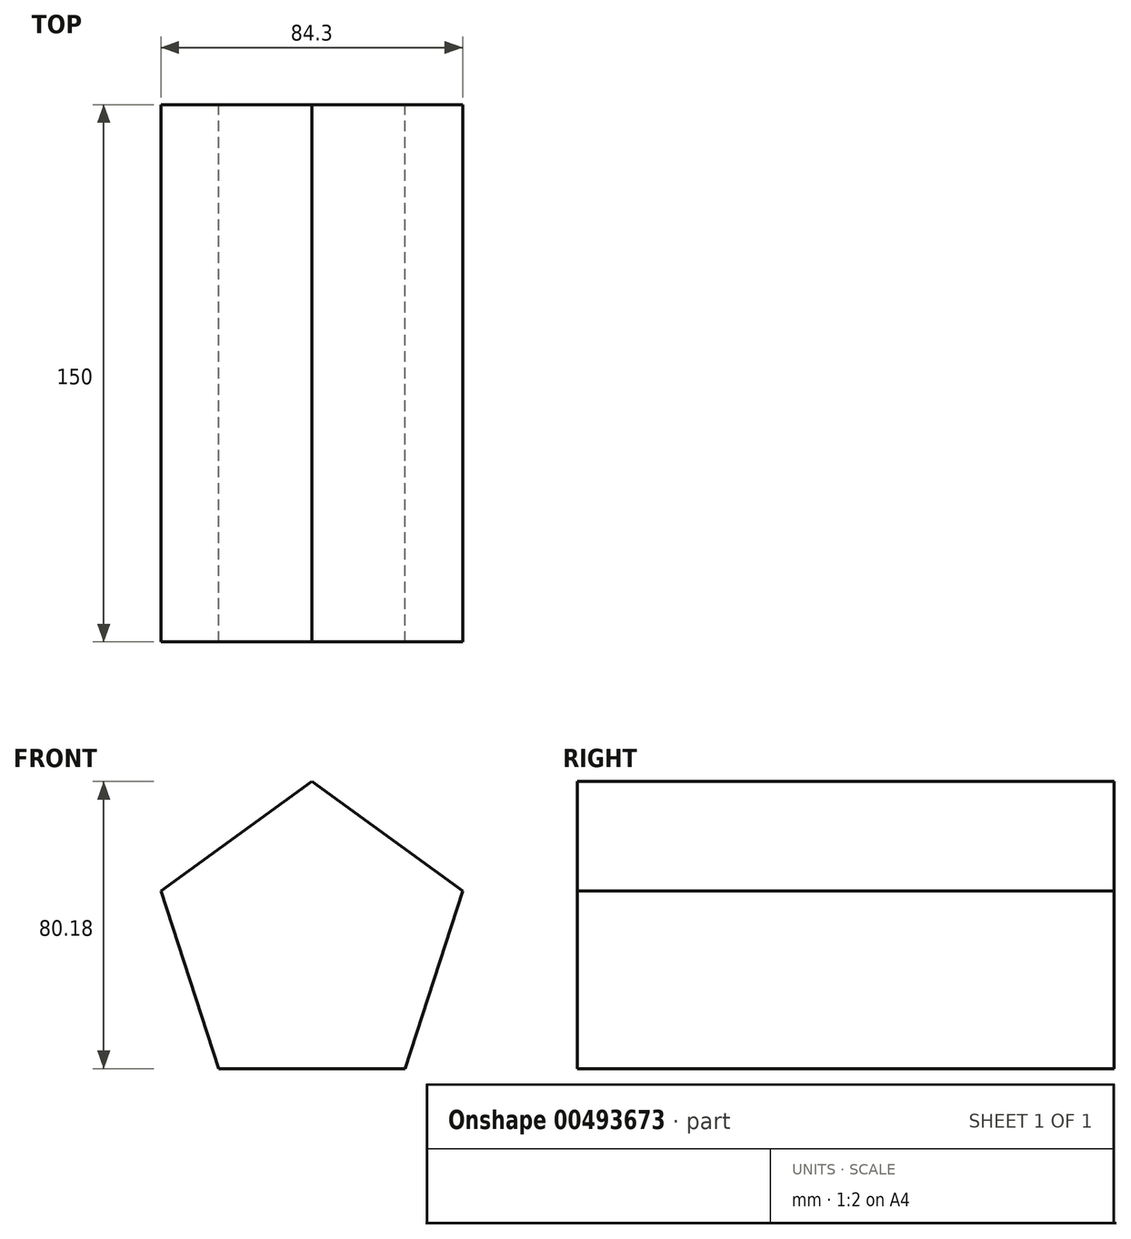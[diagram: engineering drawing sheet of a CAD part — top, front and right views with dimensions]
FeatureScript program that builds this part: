
annotation { "Feature Type Name" : "Feature", "Feature Type Description" : "" }
export const myFeature = defineFeature(function(context is Context, id is Id, definition is map)
    precondition{}
    {
        {
            var Q0;
            Q0=qCreatedBy(makeId("Front.planeOp"),FACE);
            var sketch = newSketch(context, id + "F0", { "sketchPlane" : qUnion([Q0])});
            skCircle(sketch, "E0.cCircle", {"center": v(0, 0) * mm, "radius": 44.32 * mm, "construction": true});
            skLineSegment(sketch, "E0.0", {"start": v(0, 44.32) * mm, "end": v(42.15, 13.7) * mm});
            skLineSegment(sketch, "E0.1", {"start": v(42.15, 13.7) * mm, "end": v(26.05, -35.86) * mm});
            skLineSegment(sketch, "E0.2", {"start": v(26.05, -35.86) * mm, "end": v(-26.05, -35.86) * mm});
            skLineSegment(sketch, "E0.3", {"start": v(-26.05, -35.86) * mm, "end": v(-42.15, 13.7) * mm});
            skLineSegment(sketch, "E0.4", {"start": v(-42.15, 13.7) * mm, "end": v(0, 44.32) * mm});
            skSolve(sketch);
        }
        {
            var Q0;
            Q0=makeQuery(id+"F0.imprint","IMPRINT",FACE,{"disambiguationData":[TD([[makeQuery(id+"F0.imprint","IMPRINT",EDGE,{"derivedFrom":sQuery(id+"F0.wireOp",EDGE,"E0.0")}),-1.0]])]});
            extrude(context, id + "F1", {"entities" : qUnion([Q0]), "depth" : 150 * mm});
        }
    });
